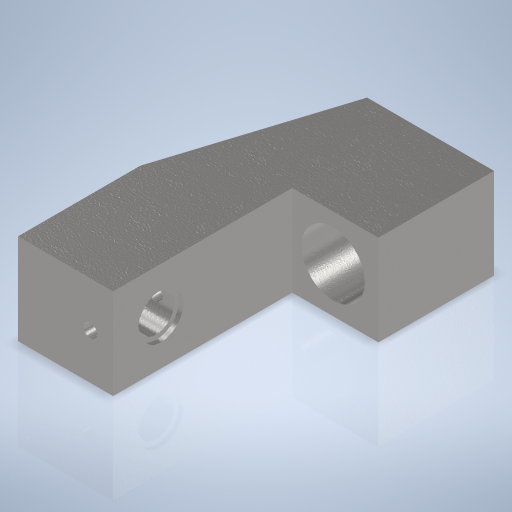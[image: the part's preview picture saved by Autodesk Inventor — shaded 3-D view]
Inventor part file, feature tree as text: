
AUTODESK INVENTOR PART (.ipt)
format: ipt  version: 2024 (Build 280153000, 153)  size: 366,080 bytes
history: native  units: mm
features: sketch x5, hole x4, plane x2, extrude x1, mirror x1, projected_geometry x1
ambient origin geometry x8: Origin, YZ Plane, XZ Plane, XY Plane, X Axis, Y Axis, Z Axis, Center Point
bodies: Volumenkörper1 (feature_tree)
feature tree (14):
  extrude  "Extrusion1"  Depth=21.0mm
  hole  "Bohrung2"  [1 undecoded]
  hole  "Bohrung3"  [1 undecoded]
  hole  "Bohrung4"  [1 undecoded]
  plane  "Arbeitsebene1"
  hole  "Bohrung7"  [1 undecoded]
  plane  "Arbeitsebene2"
  mirror  "Spiegeln2"
  sketch  "Skizze1"  dims[d0=65.0mm d1=21.0mm]
  sketch  "Skizze3"  dims[d2=39.5mm d3=38.0mm]
  sketch  "Skizze4"  dims[d4=28.0mm d5=12.0mm]
  sketch  "Skizze5"  dims[d6=20.0mm d7=0.0mm d16=10.0mm]
  sketch  "Skizze8"  dims[d17=14.0mm d18=6.0mm d19=4.0mm d20=2.0mm d21=90.0deg d22=8.0mm d23=20.594885mm d24=4.0mm d25=3.0mm d26=6.0mm d27=4.0mm d28=30.0mm d29=90.0deg d30=8.0mm d31=0.0mm d32=10.5mm d33=8.0mm d34=6.0mm d35=10.0mm d36=1.0mm d37=90.0deg d38=8.0mm d39=20.594885mm d49=12.0mm d57=14.0mm d58=2.459mm d59=6.0mm d60=4.0mm d61=2.0mm d62=90.0deg d63=9.0mm d64=20.594885mm d65=26.5mm]
  projected_geometry  "Projizierte Kontur1"
note: 4 required parameter values undecoded (feature->parameter linkage not recoverable at this tier; creation-order binding heuristic only, values carry confidence <= 0.55)
